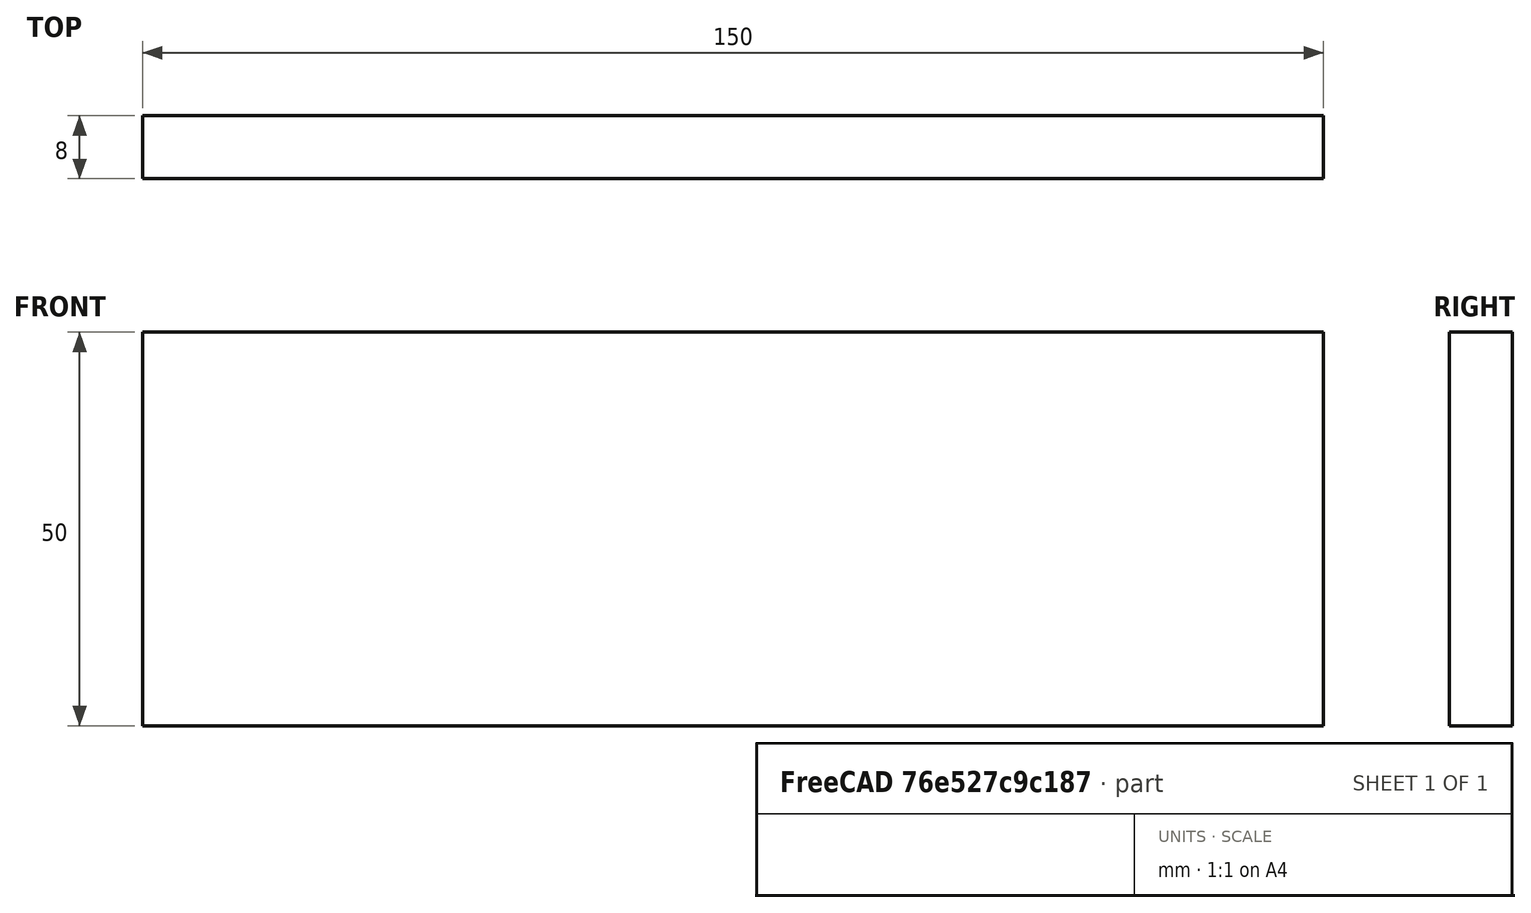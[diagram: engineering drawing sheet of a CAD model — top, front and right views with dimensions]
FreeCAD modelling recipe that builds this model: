
FCSTD DOCUMENT  (FreeCAD 0.15R4671 (Git))
Label: Flat Bar 150x8 EN10058 S235JR
License: All rights reserved
LicenseURL: http://en.wikipedia.org/wiki/All_rights_reserved
objects: Sketcher::SketchObject×1, Part::Extrusion×1
note: 2 computed .brp shape members not serialized (recipe doc carries the construction recipe); baked Part::Feature solids carry a one-line shape summary decoded from their .brp

FEATURE [Sketcher::SketchObject] Sketch
  sketch-geometry (4):
    g0: LineSegment StartX=-75 StartY=-4 StartZ=0 EndX=75 EndY=-4 EndZ=0
    g1: LineSegment StartX=75 StartY=-4 StartZ=0 EndX=75 EndY=4 EndZ=0
    g2: LineSegment StartX=75 StartY=4 StartZ=0 EndX=-75 EndY=4 EndZ=0
    g3: LineSegment StartX=-75 StartY=4 StartZ=0 EndX=-75 EndY=-4 EndZ=0
  constraints (12):
    c: Coincident(g0,g1)
    c: Coincident(g1,g2)
    c: Coincident(g2,g3)
    c: Coincident(g3,g0)
    c: Horizontal(g0)
    c: Horizontal(g2)
    c: Vertical(g1)
    c: Vertical(g3)
    c: Symmetric(g1,g2,g-2)
    c: Symmetric(g0,g1,g-1)
    c: DistanceY(g1) = 8
    c: DistanceX(g0) = 150
FEATURE [Part::Extrusion] Extrude  label="Flat Bar 150x8 EN10058 S235JR"
  Base = -> Sketch
  Dir = (0,0,50)
  Solid = true
